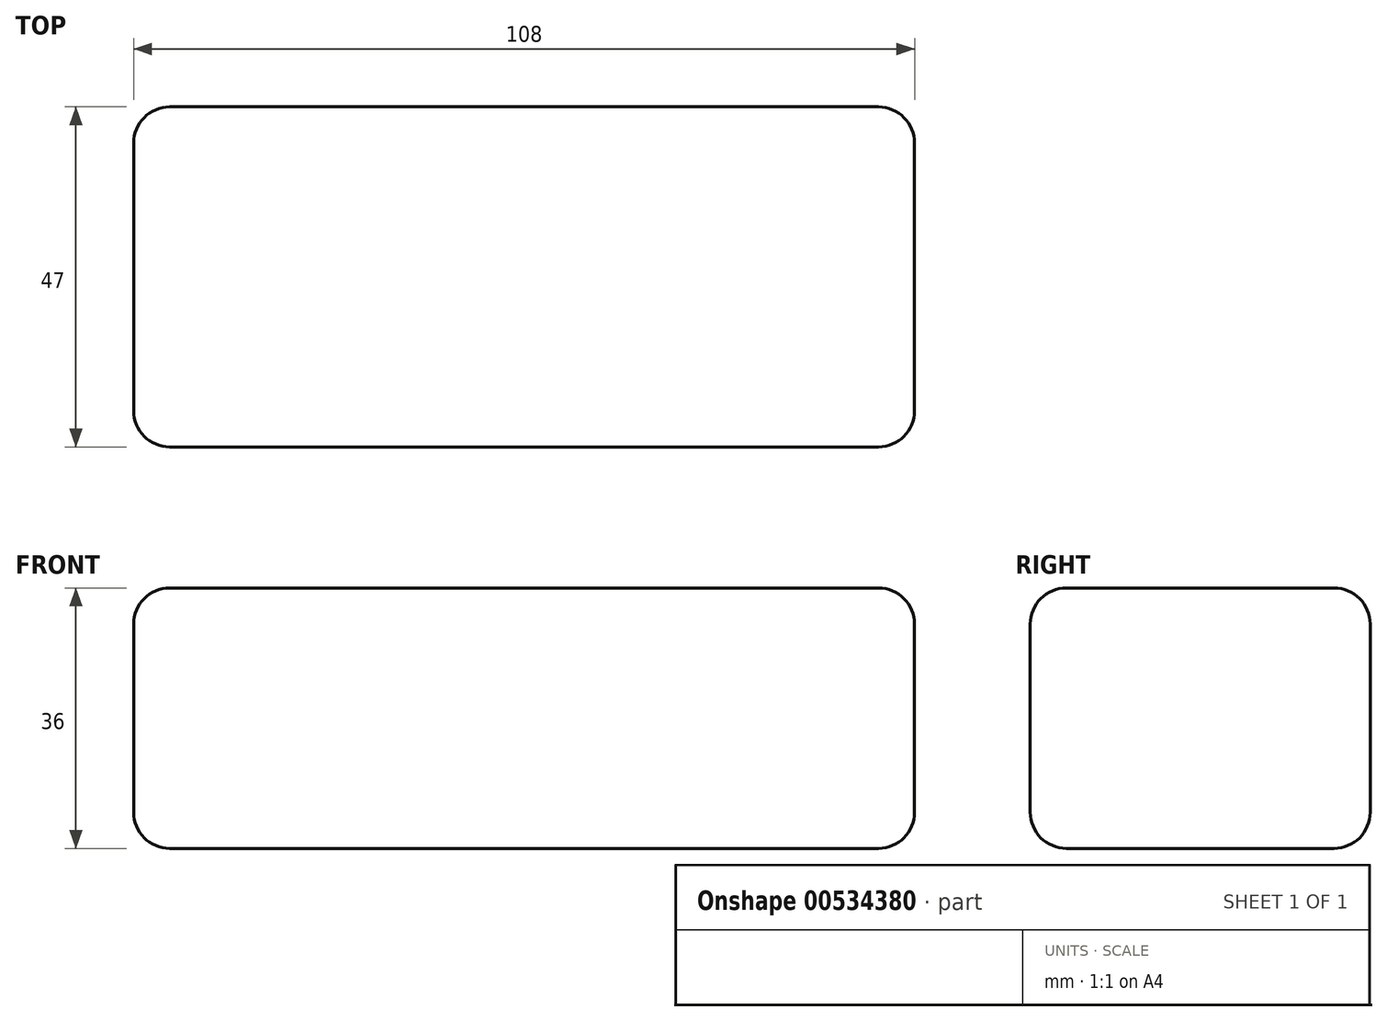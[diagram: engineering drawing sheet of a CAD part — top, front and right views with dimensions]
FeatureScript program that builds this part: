
annotation { "Feature Type Name" : "Feature", "Feature Type Description" : "" }
export const myFeature = defineFeature(function(context is Context, id is Id, definition is map)
    precondition{}
    {
        {
            var Q0;
            Q0=qCreatedBy(makeId("Top.planeOp"),FACE);
            var sketch = newSketch(context, id + "F0", { "sketchPlane" : qUnion([Q0])});
            skLineSegment(sketch, "E0.bottom", {"start": v(-58.46, 32.85) * mm, "end": v(49.54, 32.85) * mm});
            skLineSegment(sketch, "E0.top", {"start": v(-58.46, -14.15) * mm, "end": v(49.54, -14.15) * mm});
            skLineSegment(sketch, "E0.left", {"start": v(-58.46, 32.85) * mm, "end": v(-58.46, -14.15) * mm});
            skLineSegment(sketch, "E0.right", {"start": v(49.54, 32.85) * mm, "end": v(49.54, -14.15) * mm});
            skSolve(sketch);
        }
        {
            var Q0;
            Q0=makeQuery(id+"F0.imprint","IMPRINT",FACE,{"disambiguationData":[TD([[makeQuery(id+"F0.imprint","IMPRINT",EDGE,{"derivedFrom":sQuery(id+"F0.wireOp",EDGE,"E0.bottom")}),-1.0]])]});
            extrude(context, id + "F1", {"entities" : qUnion([Q0]), "depth" : 36 * mm, "offsetDistance" : 25 * mm});
        }
        {
            var Q0;
            Q0=makeQuery(id+"F1.opExtrude","CAP_EDGE",EDGE,{"disambiguationData":[OSD([sQuery(id+"F0.wireOp",EDGE,"E0.bottom")])],"isStart":false});
            var Q1;
            Q1=makeQuery(id+"F1.opExtrude","CAP_EDGE",EDGE,{"disambiguationData":[OSD([sQuery(id+"F0.wireOp",EDGE,"E0.bottom")])],"isStart":true});
            var Q2;
            Q2=makeQuery(id+"F1.opExtrude","CAP_EDGE",EDGE,{"disambiguationData":[OSD([sQuery(id+"F0.wireOp",EDGE,"E0.top")])],"isStart":false});
            var Q3;
            Q3=makeQuery(id+"F1.opExtrude","CAP_EDGE",EDGE,{"disambiguationData":[OSD([sQuery(id+"F0.wireOp",EDGE,"E0.top")])],"isStart":true});
            var Q4;
            Q4=makeQuery(id+"F1.opExtrude","CAP_EDGE",EDGE,{"disambiguationData":[OSD([sQuery(id+"F0.wireOp",EDGE,"E0.left")])],"isStart":false});
            var Q5;
            Q5=makeQuery(id+"F1.opExtrude","CAP_EDGE",EDGE,{"disambiguationData":[OSD([sQuery(id+"F0.wireOp",EDGE,"E0.left")])],"isStart":true});
            var Q6;
            Q6=makeQuery(id+"F1.opExtrude","SWEPT_EDGE",EDGE,{"disambiguationData":[OSD([sQuery(id+"F0.wireOp",EDGE,"E0.top"),sQuery(id+"F0.wireOp",EDGE,"E0.left")])]});
            var Q7;
            Q7=makeQuery(id+"F1.opExtrude","SWEPT_EDGE",EDGE,{"disambiguationData":[OSD([sQuery(id+"F0.wireOp",EDGE,"E0.bottom"),sQuery(id+"F0.wireOp",EDGE,"E0.left")])]});
            var Q8;
            Q8=makeQuery(id+"F1.opExtrude","CAP_EDGE",EDGE,{"disambiguationData":[OSD([sQuery(id+"F0.wireOp",EDGE,"E0.right")])],"isStart":false});
            var Q9;
            Q9=makeQuery(id+"F1.opExtrude","CAP_EDGE",EDGE,{"disambiguationData":[OSD([sQuery(id+"F0.wireOp",EDGE,"E0.right")])],"isStart":true});
            var Q10;
            Q10=makeQuery(id+"F1.opExtrude","SWEPT_EDGE",EDGE,{"disambiguationData":[OSD([sQuery(id+"F0.wireOp",EDGE,"E0.bottom"),sQuery(id+"F0.wireOp",EDGE,"E0.right")])]});
            var Q11;
            Q11=makeQuery(id+"F1.opExtrude","SWEPT_EDGE",EDGE,{"disambiguationData":[OSD([sQuery(id+"F0.wireOp",EDGE,"E0.top"),sQuery(id+"F0.wireOp",EDGE,"E0.right")])]});
            fillet(context, id + "F2", {"entities" : qUnion([Q0, Q1, Q2, Q3, Q4, Q5, Q6, Q7, Q8, Q9, Q10, Q11]), "radius" : 5 * mm, "tangentPropagation" : true, "allowEdgeOverflow" : false});
        }
    });
